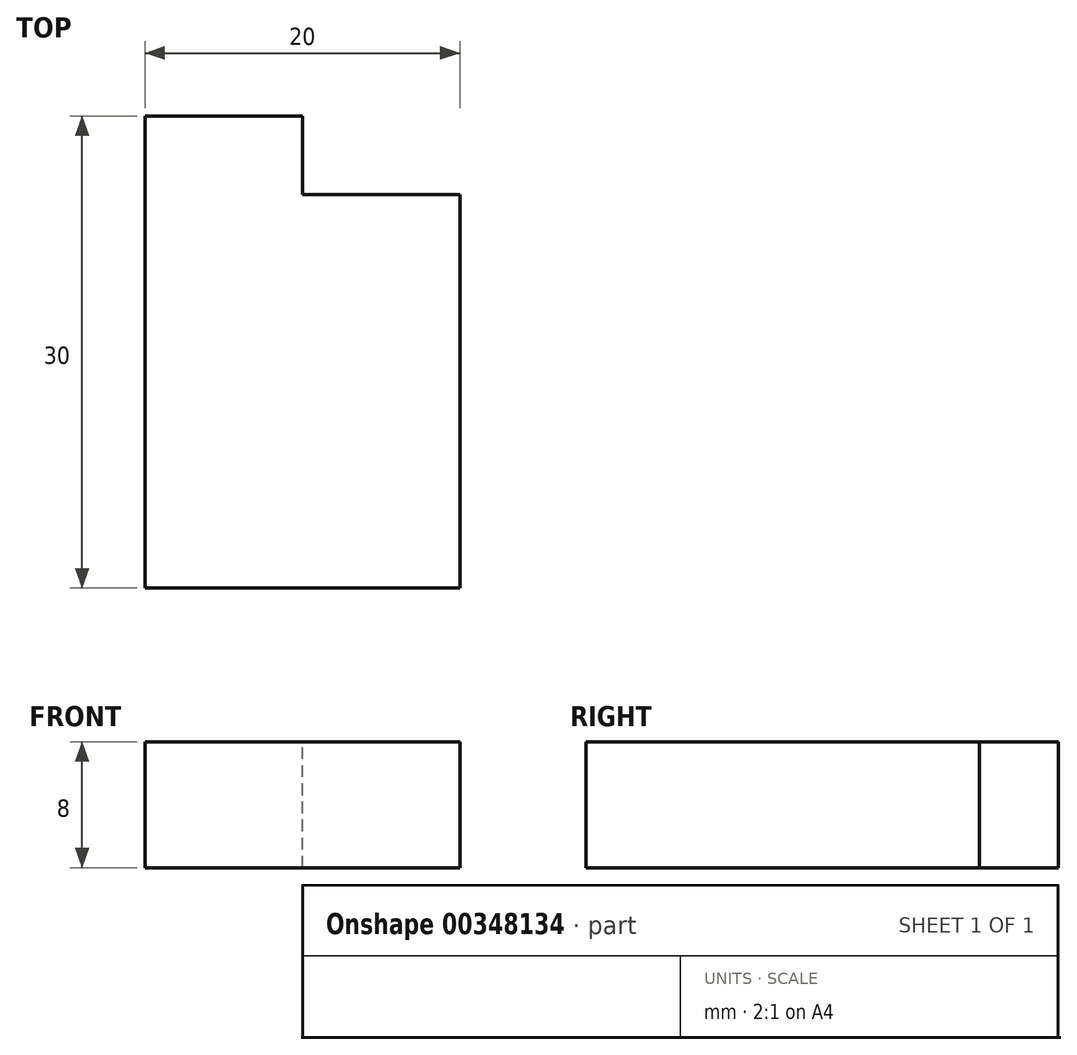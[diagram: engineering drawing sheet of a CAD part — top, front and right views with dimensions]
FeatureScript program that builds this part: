
annotation { "Feature Type Name" : "Feature", "Feature Type Description" : "" }
export const myFeature = defineFeature(function(context is Context, id is Id, definition is map)
    precondition{}
    {
        {
            var Q0;
            Q0=qCreatedBy(makeId("Top.planeOp"),FACE);
            var sketch = newSketch(context, id + "F0", { "sketchPlane" : qUnion([Q0])});
            skLineSegment(sketch, "E0.bottom", {"start": v(10, 12.5) * mm, "end": v(0, 12.5) * mm});
            skLineSegment(sketch, "E0.top", {"start": v(10, -12.5) * mm, "end": v(-10, -12.5) * mm});
            skLineSegment(sketch, "E0.left", {"start": v(10, 12.5) * mm, "end": v(10, -12.5) * mm});
            skLineSegment(sketch, "E0.right", {"start": v(-10, 12.5) * mm, "end": v(-10, -12.5) * mm});
            skPoint(sketch, "E0.middle", {"position": v(0, 0) * mm});
            skLineSegment(sketch, "E1", {"start": v(0, 12.5) * mm, "end": v(0, 17.5) * mm});
            skPoint(sketch, "E1.endSnap0", {"position": v(0, 12.5) * mm});
            skLineSegment(sketch, "E2", {"start": v(0, 17.5) * mm, "end": v(-10, 17.5) * mm});
            skLineSegment(sketch, "E3", {"start": v(-10, 17.5) * mm, "end": v(-10, 12.5) * mm});
            skSolve(sketch);
        }
        {
            var Q0;
            Q0=qCreatedBy(makeId("Front.planeOp"),FACE);
            var sketch = newSketch(context, id + "F1", { "sketchPlane" : qUnion([Q0])});
            skLineSegment(sketch, "E4", {"start": v(0, 0) * mm, "end": v(0, 8) * mm});
            skSolve(sketch);
        }
        {
            var Q0;
            Q0=makeQuery(id+"F0.imprint","IMPRINT",FACE,{"disambiguationData":[TD([[makeQuery(id+"F0.imprint","IMPRINT",EDGE,{"derivedFrom":sQuery(id+"F0.wireOp",EDGE,"E0.bottom")}),1.0]])]});
            var Q1;
            Q1=sQuery(id+"F1.wireOp",EDGE,"E4");
            sweep(context, id + "F2", {"profiles" : qUnion([Q0]), "path" : qUnion([Q1])});
        }
    });
